# Revit family: Sanitary_Showers_AXOR_36734USA-AXOR-ShowerSolutions-Porter-uni222
name_source: partatom
category: Plumbing Fixtures
revit_build: Autodesk Revit 2018 (Build: 20170223_1515(x64)
units: mm (PartAtom-declared; Revit-internal decimal feet)

## family parameters
Always vertical = No
Cut with Voids When Loaded = No
OmniClass Number = 23.31.17.19
OmniClass Title = Shower Head Fixtures
Part Type = Normal
Room Calculation Point = No
Round Connector Dimension = Use Diameter
Shared = No
Work Plane-Based = Yes

## types (5) — shared parameters
Always visible = Yes
BIMobject category = Showers
Default Elevation = 1219.2 mm
Description = AXOR ShowerSolutions Porter unit square
Edition number = 1
IFC Classification = Sanitary Terminal
Installation instructions = https://www.axor-design.com
Manufacturer = AXOR
Manufacturer name = AXOR
Material 1 = AXOR - Plastic - Gray
Model = 36734USA
OmniClass Code = 23-31 17 19
OmniClass Description = Shower Head Fixtures
Product Guid = 5e905e49-07b2-4623-92e1-f3e2e3c1ed3c
Product SKU = 36734USA
Product data url = https://www.bimobject.com
Product family = AXOR ShowerSolutions
Product group = Wall outlet
Product name = 36734USA AXOR ShowerSolutions Porter unit square
Product url = https://www.axor-design.com
QR code = https://www.bimobject.com
URL = https://www.axor-design.com
Water Inlet = 13 mm
Water Inlet Description = Water Inlet 12.7mm

## per-type parameters (varying)
| type | Material 2 |
| 821 Brushed Nickel | AXOR - Metal - 821 Brushed Nickel |
| 671 Matt Black | AXOR - Metal - 671 Matt Black |
| 341 Brushed Black Chrome | AXOR - Metal - 341 Brushed Black Chrome |
| 251 Brushed Gold Optic | AXOR - Metal - 251 Brushed Gold Optic |
| 001 Chrome | AXOR - Metal - 001 Chrome |

## geometry (parser evidence)
native form markers: Sweep x2
no freeform markers — native parametric forms only
